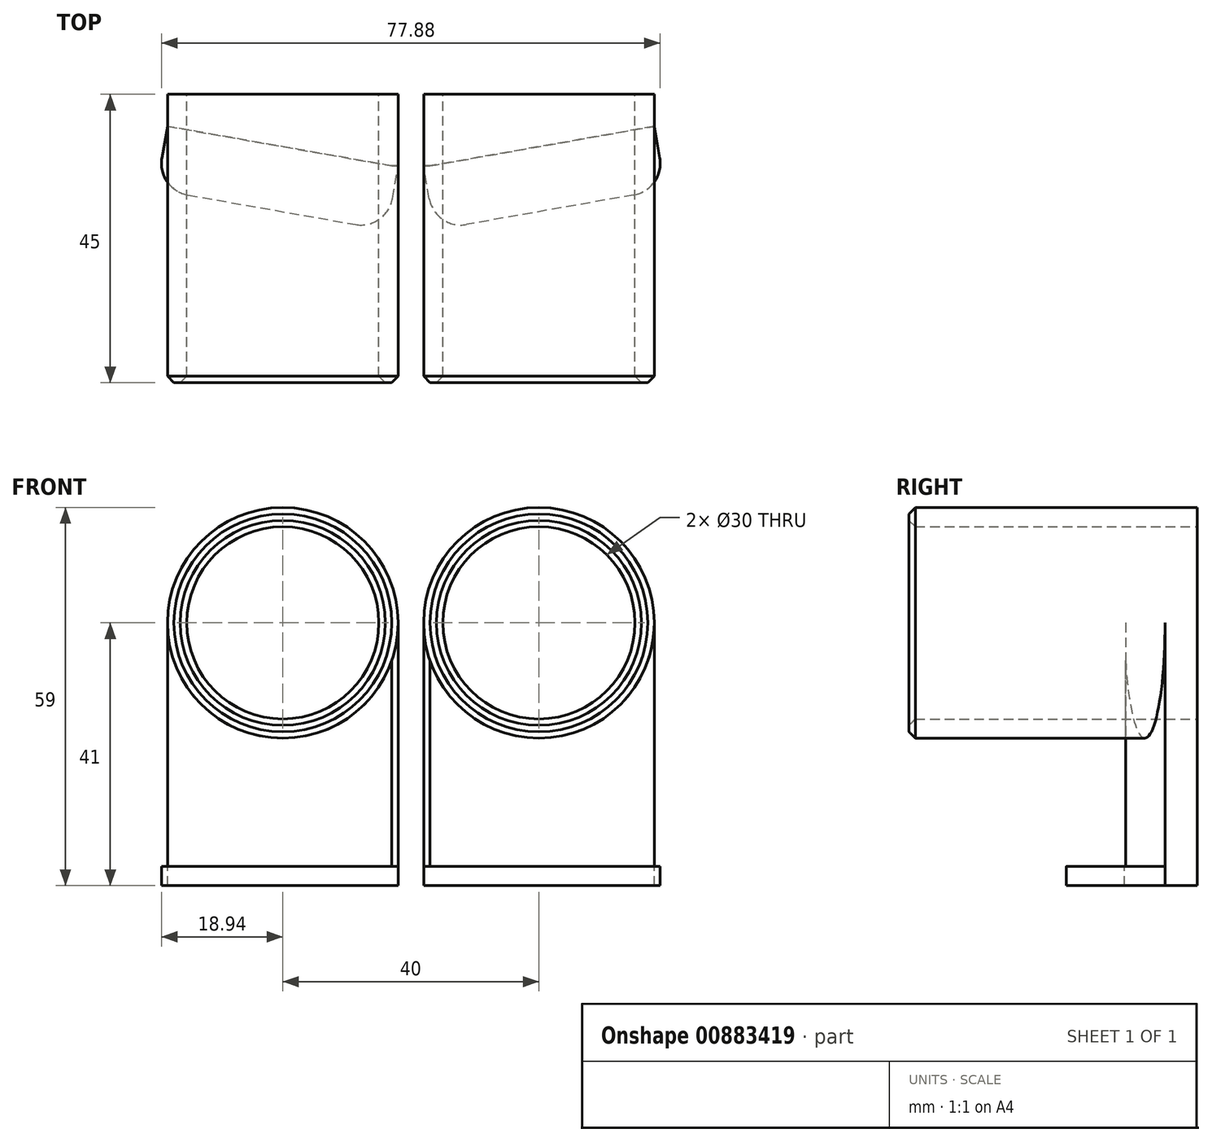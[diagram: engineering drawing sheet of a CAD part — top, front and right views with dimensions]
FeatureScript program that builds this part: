
annotation { "Feature Type Name" : "Feature", "Feature Type Description" : "" }
export const myFeature = defineFeature(function(context is Context, id is Id, definition is map)
    precondition{}
    {
        {
            var Q0;
            Q0=qCreatedBy(makeId("Front.planeOp"),FACE);
            var sketch = newSketch(context, id + "F0", { "sketchPlane" : qUnion([Q0])});
            skCircle(sketch, "E0", {"center": v(0, 0) * mm, "radius": 15 * mm});
            skCircle(sketch, "E1.0", {"center": v(0, 0) * mm, "radius": 18 * mm});
            skLineSegment(sketch, "E2", {"start": v(-18, 0) * mm, "end": v(-18, -38) * mm});
            skLineSegment(sketch, "E3", {"start": v(-18, -38) * mm, "end": v(18, -38) * mm});
            skLineSegment(sketch, "E4", {"start": v(18, -38) * mm, "end": v(18, 0) * mm});
            skSolve(sketch);
        }
        {
            var Q0;
            Q0=makeQuery(id+"F0.imprint","IMPRINT",FACE,{"disambiguationData":[TD([[makeQuery(id+"F0.imprint","IMPRINT",EDGE,{"derivedFrom":sQuery(id+"F0.wireOp",EDGE,"E0")}),-1.0]])]});
            extrude(context, id + "F1", {"entities" : qUnion([Q0]), "depth" : 45 * mm, "offsetDistance" : 25 * mm});
        }
        {
            var Q0;
            Q0 = qSketchRegion(id + "F0", true);
            extrude(context, id + "F2", {"entities" : qUnion([Q0]), "operationType" : NewBodyOperationType.ADD, "depth" : 5 * mm, "offsetDistance" : 25 * mm});
        }
        {
            var Q0;
            Q0=makeQuery(id+"F2.opExtrude","SWEPT_FACE",FACE,{"disambiguationData":[OSD([sQuery(id+"F0.wireOp",EDGE,"E3")])]});
            var sketch = newSketch(context, id + "F3", { "sketchPlane" : qUnion([Q0])});
            skLineSegment(sketch, "E5", {"start": v(-18, 0) * mm, "end": v(-18, 5) * mm});
            skLineSegment(sketch, "E6", {"start": v(-18, 5) * mm, "end": v(-19.74, 14.85) * mm});
            skLineSegment(sketch, "E7", {"start": v(-19.74, 14.85) * mm, "end": v(16.26, 21.2) * mm});
            skLineSegment(sketch, "E8", {"start": v(16.26, 21.2) * mm, "end": v(18, 11.35) * mm});
            skLineSegment(sketch, "E9", {"start": v(18, 11.35) * mm, "end": v(18, 0) * mm});
            skLineSegment(sketch, "E10", {"start": v(18, 0) * mm, "end": v(-18, 0) * mm});
            skLineSegment(sketch, "E11", {"start": v(-18, 5) * mm, "end": v(18, 11.35) * mm});
            skSolve(sketch);
        }
        {
            var Q0;
            Q0 = qSketchRegion(id + "F3", true);
            extrude(context, id + "F4", {"entities" : qUnion([Q0]), "operationType" : NewBodyOperationType.ADD, "depth" : 3 * mm, "offsetDistance" : 25 * mm});
        }
        {
            var Q0;
            Q0=makeQuery(id+"F4.opExtrude","CAP_FACE",FACE,{"disambiguationData":[OSD([sQuery(id+"F3.wireOp",EDGE,"E5"),sQuery(id+"F3.wireOp",EDGE,"E6"),sQuery(id+"F3.wireOp",EDGE,"E7"),sQuery(id+"F3.wireOp",EDGE,"E8"),sQuery(id+"F3.wireOp",EDGE,"E9"),sQuery(id+"F3.wireOp",EDGE,"E10")])],"isStart":false});
            var sketch = newSketch(context, id + "F5", { "sketchPlane" : qUnion([Q0])});
            skLineSegment(sketch, "E12.0", {"start": v(-18, 0) * mm, "end": v(-18, 5) * mm});
            skLineSegment(sketch, "E12.4", {"start": v(18, 11.35) * mm, "end": v(18, 0) * mm});
            skLineSegment(sketch, "E12.5", {"start": v(18, 0) * mm, "end": v(-18, 0) * mm});
            skLineSegment(sketch, "E12.6", {"start": v(-18, 5) * mm, "end": v(18, 11.35) * mm});
            skSolve(sketch);
        }
        {
            var Q0;
            Q0 = qSketchRegion(id + "F5", true);
            var Q1;
            Q1=makeQuery(id+"F1.opExtrude","SWEPT_FACE",FACE,{"disambiguationData":[OSD([sQuery(id+"F0.wireOp",EDGE,"E1.0")])]});
            extrude(context, id + "F6", {"entities" : qUnion([Q0]), "operationType" : NewBodyOperationType.ADD, "endBound" : BoundingType.UP_TO_SURFACE, "oppositeDirection" : true, "depth" : 25 * mm, "endBoundEntityFace" : qUnion([Q1]), "offsetDistance" : 25 * mm});
        }
        {
            var Q0;
            Q0=makeQuery(id+"F1.opExtrude","CAP_EDGE",EDGE,{"disambiguationData":[OSD([sQuery(id+"F0.wireOp",EDGE,"E0")])],"isStart":false});
            var Q1;
            Q1=makeQuery(id+"F1.opExtrude","CAP_EDGE",EDGE,{"disambiguationData":[OSD([sQuery(id+"F0.wireOp",EDGE,"E1.0")])],"isStart":false});
            chamfer(context, id + "F7", {"entities" : qUnion([Q0, Q1]), "width" : 1 * mm, "tangentPropagation" : true});
        }
        {
            var Q0;
            Q0=makeQuery(id+"F4.opExtrude","SWEPT_EDGE",EDGE,{"disambiguationData":[OSD([sQuery(id+"F3.wireOp",EDGE,"E7"),sQuery(id+"F3.wireOp",EDGE,"E8")])]});
            var Q1;
            Q1=makeQuery(id+"F4.opExtrude","SWEPT_EDGE",EDGE,{"disambiguationData":[OSD([sQuery(id+"F3.wireOp",EDGE,"E6"),sQuery(id+"F3.wireOp",EDGE,"E7")])]});
            fillet(context, id + "F8", {"entities" : qUnion([Q0, Q1]), "radius" : 5 * mm, "tangentPropagation" : true, "allowEdgeOverflow" : false});
        }
        {
            var Q0;
            Q0=makeQuery(id+"F6.opExtrude","SWEPT_EDGE",EDGE,{"disambiguationData":[OSD([sQuery(id+"F3.wireOp",EDGE,"E8"),sQuery(id+"F5.wireOp",EDGE,"E12.4"),sQuery(id+"F5.wireOp",EDGE,"E12.6")])]});
            chamfer(context, id + "F9", {"entities" : qUnion([Q0]), "chamferType" : ChamferType.OFFSET_ANGLE, "width" : 1 * mm, "oppositeDirection" : true, "angle" : 10 * degree, "tangentPropagation" : true});
        }
        {
            var Q0;
            Q0=qCreatedBy(makeId("Right.planeOp"),FACE);
            cPlane(context, id + "F10", {"entities" : qUnion([Q0]), "cplaneType" : CPlaneType.OFFSET, "offset" : 20 * mm, "width" : 150 * mm, "height" : 150 * mm});
        }
        {
            var Q0;
            Q0=makeQuery(id+"F1.opExtrude","SWEPT_BODY",BODY,{"disambiguationData":[OSD([sQuery(id+"F0.wireOp",EDGE,"E0"),sQuery(id+"F0.wireOp",EDGE,"E1.0")])]});
            var Q1;
            Q1=qCreatedBy(id+"F10.planeOp",FACE);
            mirror(context, id + "F11", {"entities" : qUnion([Q0]), "mirrorPlane" : qUnion([Q1])});
        }
    });
